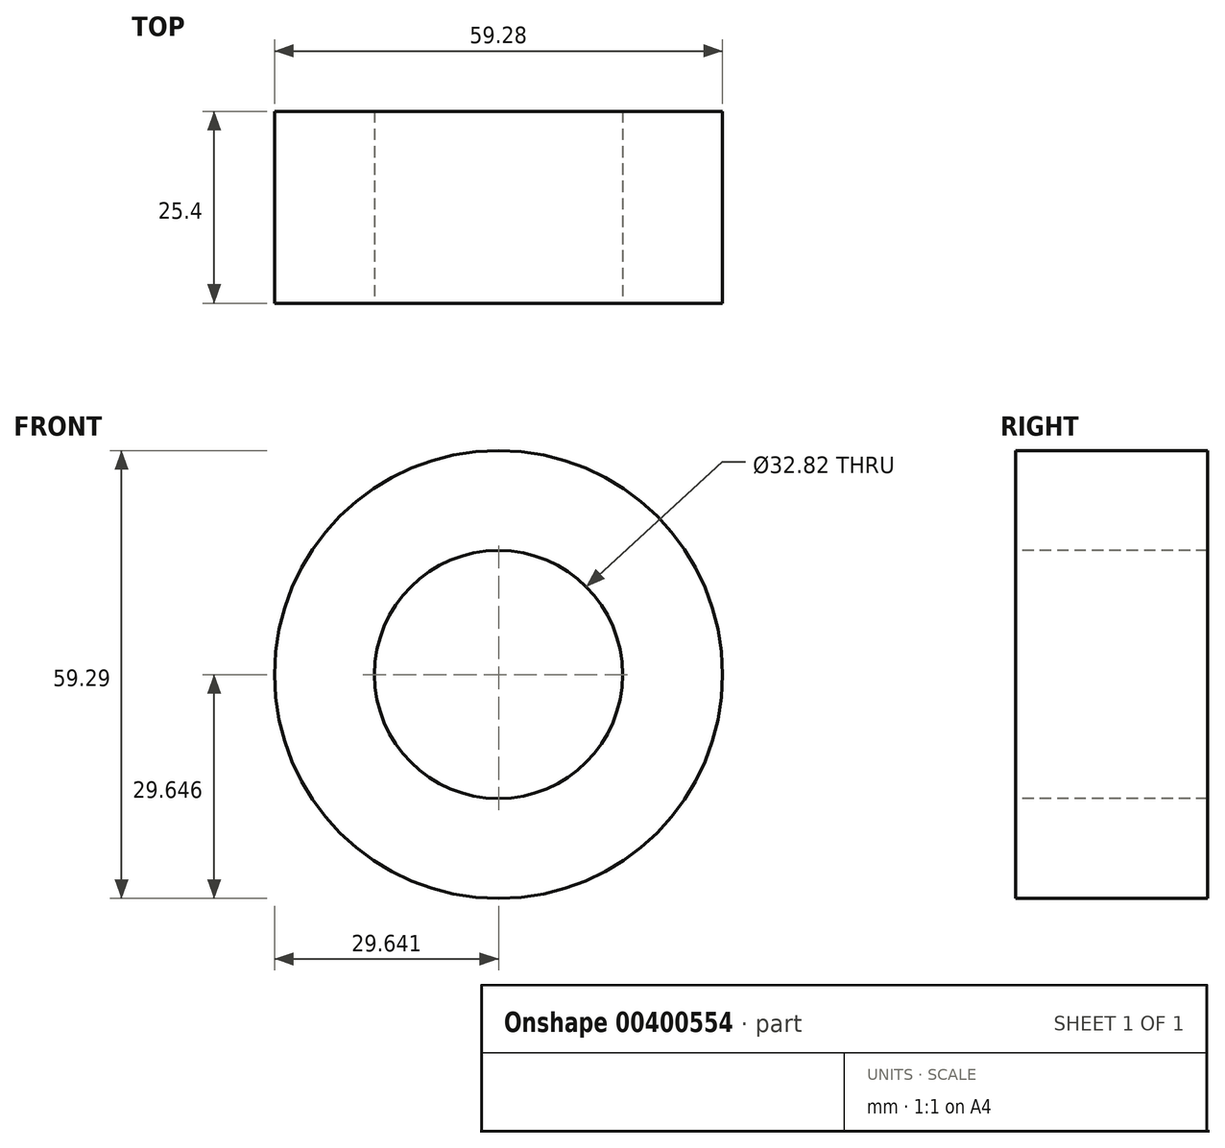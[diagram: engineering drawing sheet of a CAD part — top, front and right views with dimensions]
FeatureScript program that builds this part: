
annotation { "Feature Type Name" : "Feature", "Feature Type Description" : "" }
export const myFeature = defineFeature(function(context is Context, id is Id, definition is map)
    precondition{}
    {
        {
            var Q0;
            Q0=qCreatedBy(makeId("Front.planeOp"),FACE);
            var sketch = newSketch(context, id + "F0", { "sketchPlane" : qUnion([Q0])});
            skCircle(sketch, "E0", {"center": v(-18.92, 10.3) * mm, "radius": 29.64 * mm});
            skCircle(sketch, "E1", {"center": v(-18.92, 10.3) * mm, "radius": 16.41 * mm});
            skSolve(sketch);
        }
        {
            var Q0;
            Q0=makeQuery(id+"F0.imprint","IMPRINT",FACE,{"disambiguationData":[TD([[makeQuery(id+"F0.imprint","IMPRINT",EDGE,{"derivedFrom":sQuery(id+"F0.wireOp",EDGE,"E0")}),1.0]])]});
            extrude(context, id + "F1", {"entities" : qUnion([Q0]), "oppositeDirection" : true, "depth" : 25.4 * mm});
        }
    });
